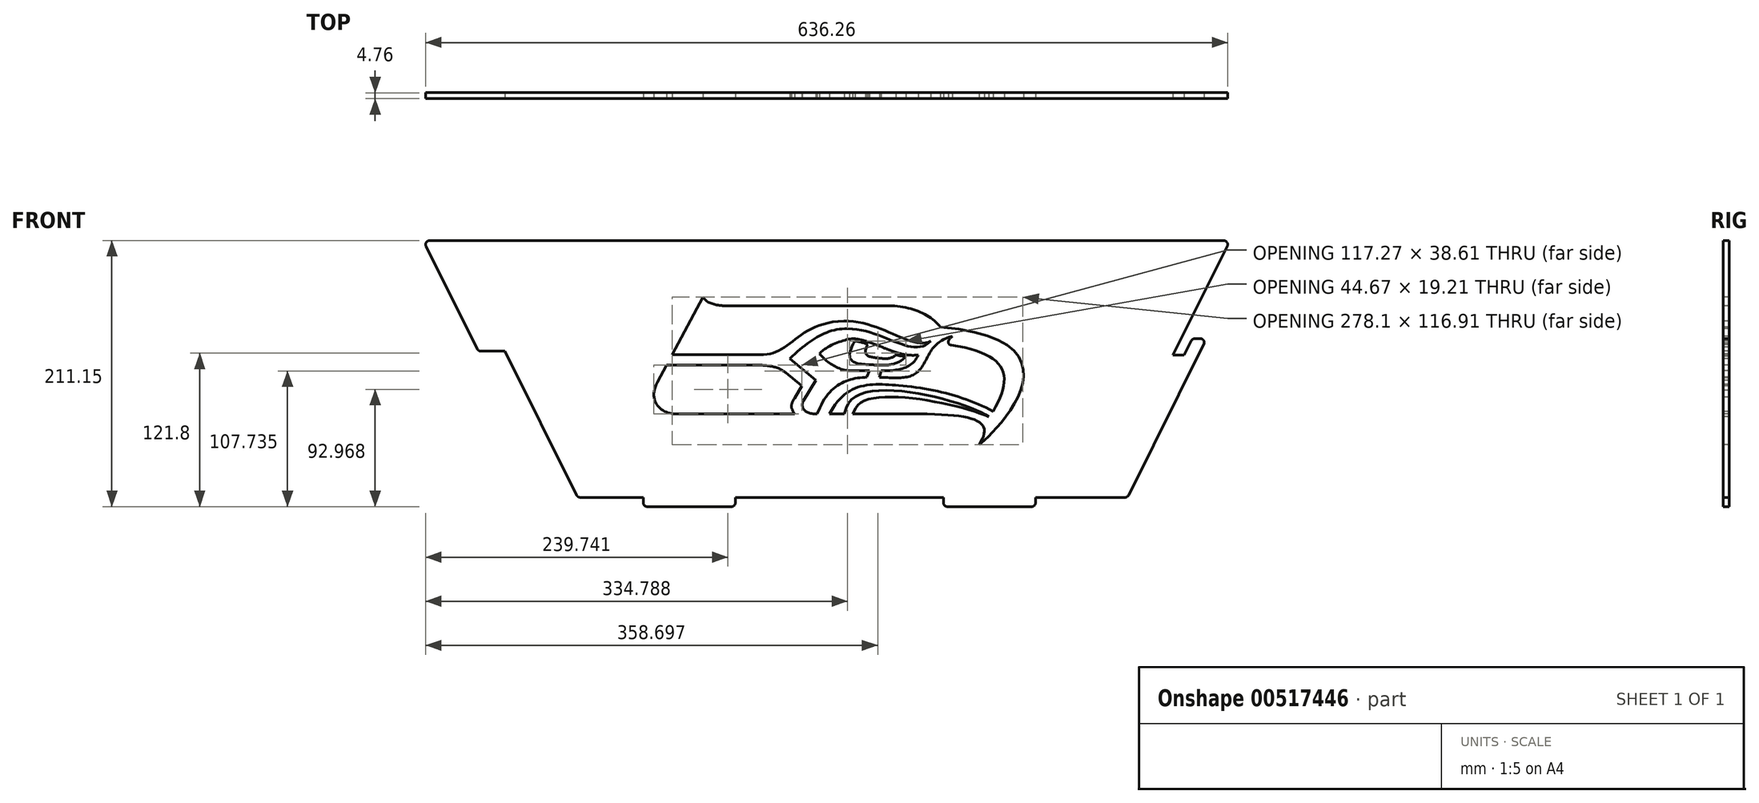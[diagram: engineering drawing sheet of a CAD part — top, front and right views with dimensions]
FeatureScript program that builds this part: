
annotation { "Feature Type Name" : "Feature", "Feature Type Description" : "" }
export const myFeature = defineFeature(function(context is Context, id is Id, definition is map)
    precondition{}
    {
        {
            var Q0;
            Q0=qCreatedBy(makeId("Front.planeOp"),FACE);
            var sketch = newSketch(context, id + "F0", { "sketchPlane" : qUnion([Q0])});
            skLineSegment(sketch, "E0", {"start": v(-309.98, 203.78) * mm, "end": v(304.85, 203.78) * mm});
            skLineSegment(sketch, "E1", {"start": v(289.12, 121.39) * mm, "end": v(229.48, 1.76) * mm});
            skLineSegment(sketch, "E2", {"start": v(226.64, 0) * mm, "end": v(155.58, 0) * mm});
            skLineSegment(sketch, "E3", {"start": v(0, 0) * mm, "end": v(0, 203.78) * mm, "construction": true});
            skLineSegment(sketch, "E4", {"start": v(-155.58, 0) * mm, "end": v(-155.58, -4.2) * mm});
            skLineSegment(sketch, "E5", {"start": v(-152.4, -7.37) * mm, "end": v(-85.73, -7.37) * mm});
            skLineSegment(sketch, "E6", {"start": v(-82.55, -4.2) * mm, "end": v(-82.55, 0) * mm});
            skLineSegment(sketch, "E7", {"start": v(82.55, 0) * mm, "end": v(82.55, -4.2) * mm});
            skLineSegment(sketch, "E8", {"start": v(85.73, -7.37) * mm, "end": v(152.4, -7.37) * mm});
            skLineSegment(sketch, "E9", {"start": v(155.58, -4.2) * mm, "end": v(155.58, 0) * mm});
            skLineSegment(sketch, "E10", {"start": v(279.18, 124.22) * mm, "end": v(273.51, 112.85) * mm});
            skLineSegment(sketch, "E11", {"start": v(273.51, 112.85) * mm, "end": v(264.64, 112.85) * mm});
            skLineSegment(sketch, "E12", {"start": v(264.64, 112.85) * mm, "end": v(307.69, 199.19) * mm});
            skLineSegment(sketch, "E13", {"start": v(282.02, 125.98) * mm, "end": v(286.28, 125.98) * mm});
            skArc(sketch, "E14.filletArc", {"start": v(282.02, 125.98) * mm, "mid": v(280.35, 125.5) * mm, "end": v(279.18, 124.22) * mm});
            skArc(sketch, "E15.filletArc", {"start": v(289.12, 121.39) * mm, "mid": v(288.98, 124.47) * mm, "end": v(286.28, 125.98) * mm});
            skLineSegment(sketch, "E16", {"start": v(-284.48, 116.03) * mm, "end": v(-265.5, 116.03) * mm});
            skLineSegment(sketch, "E17", {"start": v(-287.33, 117.79) * mm, "end": v(-327.91, 199.19) * mm});
            skLineSegment(sketch, "E18", {"start": v(-309.98, 203.78) * mm, "end": v(-325.07, 203.78) * mm});
            skLineSegment(sketch, "E19", {"start": v(264.64, 112.85) * mm, "end": v(-263.91, 112.85) * mm, "construction": true});
            skPoint(sketch, "E20.visualSharp", {"position": v(-330.2, 203.78) * mm});
            skArc(sketch, "E20.filletArc", {"start": v(-325.07, 203.78) * mm, "mid": v(-327.77, 202.27) * mm, "end": v(-327.91, 199.19) * mm});
            skPoint(sketch, "E21.visualSharp", {"position": v(-286.45, 116.03) * mm});
            skArc(sketch, "E21.filletArc", {"start": v(-287.33, 117.79) * mm, "mid": v(-286.16, 116.5) * mm, "end": v(-284.48, 116.03) * mm});
            skLineSegment(sketch, "E22", {"start": v(-286.45, 116.03) * mm, "end": v(-228.6, 0) * mm, "construction": true});
            skLineSegment(sketch, "E23", {"start": v(-309.24, 203.78) * mm, "end": v(-208.52, 1.76) * mm, "construction": true});
            skLineSegment(sketch, "E24", {"start": v(-228.6, 0) * mm, "end": v(-207.64, 0) * mm, "construction": true});
            skLineSegment(sketch, "E25.trimOffspring", {"start": v(-155.58, 0) * mm, "end": v(-205.68, 0) * mm});
            skLineSegment(sketch, "E26.trimOffspring", {"start": v(82.55, 0) * mm, "end": v(-82.55, 0) * mm});
            skLineSegment(sketch, "E27", {"start": v(-265.5, 116.03) * mm, "end": v(-207.64, 0) * mm});
            skPoint(sketch, "E28.visualSharp", {"position": v(-155.58, -7.37) * mm});
            skArc(sketch, "E28.filletArc", {"start": v(-155.58, -4.2) * mm, "mid": v(-154.65, -6.44) * mm, "end": v(-152.4, -7.37) * mm});
            skPoint(sketch, "E29.visualSharp", {"position": v(-82.55, -7.37) * mm});
            skArc(sketch, "E29.filletArc", {"start": v(-85.73, -7.37) * mm, "mid": v(-83.48, -6.44) * mm, "end": v(-82.55, -4.2) * mm});
            skPoint(sketch, "E30.visualSharp", {"position": v(82.55, -7.37) * mm});
            skArc(sketch, "E30.filletArc", {"start": v(82.55, -4.2) * mm, "mid": v(83.48, -6.44) * mm, "end": v(85.73, -7.37) * mm});
            skPoint(sketch, "E31.visualSharp", {"position": v(155.58, -7.37) * mm});
            skArc(sketch, "E31.filletArc", {"start": v(152.4, -7.37) * mm, "mid": v(154.65, -6.44) * mm, "end": v(155.58, -4.2) * mm});
            skPoint(sketch, "E32.visualSharp", {"position": v(-207.64, 0) * mm});
            skPoint(sketch, "E33.visualSharp", {"position": v(228.6, 0) * mm});
            skPoint(sketch, "E34.visualSharp", {"position": v(309.98, 203.78) * mm});
            skArc(sketch, "E34.filletArc", {"start": v(307.69, 199.19) * mm, "mid": v(307.55, 202.27) * mm, "end": v(304.85, 203.78) * mm});
            skLineSegment(sketch, "E35", {"start": v(289.12, 121.39) * mm, "end": v(330.2, 203.78) * mm, "construction": true});
            skLineSegment(sketch, "E36", {"start": v(330.2, 203.78) * mm, "end": v(304.85, 203.78) * mm, "construction": true});
            skArc(sketch, "E37.filletArc", {"start": v(226.64, 0) * mm, "mid": v(228.3, 0.48) * mm, "end": v(229.48, 1.76) * mm});
            skArc(sketch, "E38.filletArc", {"start": v(-208.52, 1.76) * mm, "mid": v(-207.35, 0.48) * mm, "end": v(-205.68, 0) * mm});
            skSolve(sketch);
        }
        {
            var Q0;
            Q0 = qSketchRegion(id + "F0", true);
            extrude(context, id + "F1", {"entities" : qUnion([Q0]), "oppositeDirection" : true, "depth" : 4.76 * mm, "offsetDistance" : 25.4 * mm});
        }
        {
            var Q0;
            Q0=makeQuery(id+"F1.opExtrude","CAP_FACE",FACE,{"disambiguationData":[OSD([sQuery(id+"F0.wireOp",EDGE,"E0"),sQuery(id+"F0.wireOp",EDGE,"E1"),sQuery(id+"F0.wireOp",EDGE,"E2"),sQuery(id+"F0.wireOp",EDGE,"E4"),sQuery(id+"F0.wireOp",EDGE,"E5"),sQuery(id+"F0.wireOp",EDGE,"E6"),sQuery(id+"F0.wireOp",EDGE,"E7"),sQuery(id+"F0.wireOp",EDGE,"E8"),sQuery(id+"F0.wireOp",EDGE,"E9"),sQuery(id+"F0.wireOp",EDGE,"E10"),sQuery(id+"F0.wireOp",EDGE,"E11"),sQuery(id+"F0.wireOp",EDGE,"E12"),sQuery(id+"F0.wireOp",EDGE,"E13"),sQuery(id+"F0.wireOp",EDGE,"E14.filletArc"),sQuery(id+"F0.wireOp",EDGE,"E15.filletArc"),sQuery(id+"F0.wireOp",EDGE,"E16"),sQuery(id+"F0.wireOp",EDGE,"E17"),sQuery(id+"F0.wireOp",EDGE,"E18"),sQuery(id+"F0.wireOp",EDGE,"E20.filletArc"),sQuery(id+"F0.wireOp",EDGE,"E21.filletArc"),sQuery(id+"F0.wireOp",EDGE,"E25.trimOffspring"),sQuery(id+"F0.wireOp",EDGE,"E26.trimOffspring"),sQuery(id+"F0.wireOp",EDGE,"E27"),sQuery(id+"F0.wireOp",EDGE,"E28.filletArc"),sQuery(id+"F0.wireOp",EDGE,"E29.filletArc"),sQuery(id+"F0.wireOp",EDGE,"E30.filletArc"),sQuery(id+"F0.wireOp",EDGE,"E31.filletArc"),sQuery(id+"F0.wireOp",EDGE,"E34.filletArc")])],"isStart":true});
            var sketch = newSketch(context, id + "F2", { "sketchPlane" : qUnion([Q0])});
            skLineSegment(sketch, "E39", {"start": v(0, 0) * mm, "end": v(0, 203.78) * mm, "construction": true});
            skLineSegment(sketch, "E40", {"start": v(0, 167.71) * mm, "end": v(0, 33.27) * mm, "construction": true});
            skLineSegment(sketch, "E41", {"start": v(-108.09, 158.82) * mm, "end": v(-132.5, 113.35) * mm});
            skLineSegment(sketch, "E42", {"start": v(-130.23, 66.3) * mm, "end": v(-35.6, 66.3) * mm});
            skLineSegment(sketch, "E43", {"start": v(39.49, 151.96) * mm, "end": v(-89.13, 151.96) * mm});
            skFitSpline(sketch, "E44", {"points": [v(-144.4, 91.19) * mm, v(-130.23, 66.3) * mm], "startDerivative": vector(-23.62, -43.99) * mm, "endDerivative": vector(34.53, 0) * mm});
            skFitSpline(sketch, "E45", {"points": [v(-108.09, 158.82) * mm, v(-89.13, 151.96) * mm], "startDerivative": vector(9.52, -18.99) * mm, "endDerivative": vector(11.02, 0) * mm});
            skFitSpline(sketch, "E46", {"points": [v(39.49, 151.96) * mm, v(80.15, 135.2) * mm], "startDerivative": vector(51.44, 0) * mm, "endDerivative": vector(23.97, -30.42) * mm});
            skFitSpline(sketch, "E47", {"points": [v(80.15, 135.2) * mm, v(110.88, 41.9) * mm], "startDerivative": vector(360.12, -30.49) * mm, "endDerivative": vector(-33.86, -25.2) * mm});
            skFitSpline(sketch, "E48", {"points": [v(56.6, 66.3) * mm, v(110.88, 41.9) * mm], "startDerivative": vector(161.76, 0) * mm, "endDerivative": vector(-35.05, -56.56) * mm});
            skLineSegment(sketch, "E49", {"start": v(-137.04, 104.9) * mm, "end": v(-63.89, 104.9) * mm});
            skFitSpline(sketch, "E50", {"points": [v(-63.89, 104.9) * mm, v(-42.6, 98.92) * mm], "startDerivative": vector(29.3, 0) * mm, "endDerivative": vector(14.25, -11.8) * mm});
            skLineSegment(sketch, "E51", {"start": v(-42.6, 98.92) * mm, "end": v(-29.87, 88.38) * mm});
            skLineSegment(sketch, "E52", {"start": v(-29.87, 88.38) * mm, "end": v(-35.6, 78.74) * mm});
            skFitSpline(sketch, "E53", {"points": [v(-35.6, 78.74) * mm, v(-35.6, 66.3) * mm], "startDerivative": vector(-10.08, -16.94) * mm, "endDerivative": vector(9.5, -15.27) * mm});
            skLineSegment(sketch, "E54", {"start": v(-132.5, 113.35) * mm, "end": v(-60.21, 113.35) * mm});
            skLineSegment(sketch, "E55.trimOffspring", {"start": v(-137.04, 104.9) * mm, "end": v(-144.4, 91.19) * mm});
            skLineSegment(sketch, "E56", {"start": v(-132.5, 113.35) * mm, "end": v(-137.04, 104.9) * mm, "construction": true});
            skFitSpline(sketch, "E57", {"points": [v(-60.21, 113.35) * mm, v(3.5, 139.84) * mm], "startDerivative": vector(63.1, 0) * mm, "endDerivative": vector(107.2, 1.94) * mm});
            skFitSpline(sketch, "E58", {"points": [v(3.5, 139.84) * mm, v(72.6, 124.07) * mm], "startDerivative": vector(90.38, 1.64) * mm, "endDerivative": vector(45.22, 23.83) * mm});
            skFitSpline(sketch, "E59", {"points": [v(72.6, 124.07) * mm, v(6.52, 133.86) * mm], "startDerivative": vector(-45.64, -45.32) * mm, "endDerivative": vector(-85.94, 0.42) * mm});
            skFitSpline(sketch, "E60", {"points": [v(6.52, 133.86) * mm, v(-39.46, 110.17) * mm], "startDerivative": vector(-51.76, 0.25) * mm, "endDerivative": vector(-48.45, -45.08) * mm});
            skLineSegment(sketch, "E61", {"start": v(-39.46, 110.17) * mm, "end": v(-18.8, 93.06) * mm});
            skLineSegment(sketch, "E62", {"start": v(-18.8, 93.06) * mm, "end": v(-28.53, 76.72) * mm});
            skFitSpline(sketch, "E63", {"points": [v(-28.53, 76.72) * mm, v(-19.85, 66.3) * mm], "startDerivative": vector(-7.73, -12.98) * mm, "endDerivative": vector(25.06, 0) * mm});
            skLineSegment(sketch, "E64.trimOffspring", {"start": v(-19.85, 66.3) * mm, "end": v(-17.7, 66.3) * mm});
            skLineSegment(sketch, "E65", {"start": v(-35.6, 66.3) * mm, "end": v(-19.85, 66.3) * mm, "construction": true});
            skLineSegment(sketch, "E66", {"start": v(-15.54, 71.12) * mm, "end": v(-4.96, 71.12) * mm});
            skFitSpline(sketch, "E67", {"points": [v(12.96, 71.12) * mm, v(118.51, 64.03) * mm], "startDerivative": vector(28.3, 55.79) * mm, "endDerivative": vector(66.83, -29.51) * mm});
            skFitSpline(sketch, "E68", {"points": [v(118.51, 64.03) * mm, v(5.37, 71.12) * mm], "startDerivative": vector(-50.89, 35.62) * mm, "endDerivative": vector(-29.24, -87.9) * mm});
            skLineSegment(sketch, "E69.trimOffspring", {"start": v(5.37, 71.12) * mm, "end": v(12.96, 71.12) * mm});
            skFitSpline(sketch, "E70", {"points": [v(121.98, 68.24) * mm, v(88.5, 120.82) * mm], "startDerivative": vector(50.2, 86.85) * mm, "endDerivative": vector(-135.02, 20.7) * mm});
            skFitSpline(sketch, "E71", {"points": [v(88.5, 120.82) * mm, v(89.53, 127.83) * mm], "startDerivative": vector(-5.03, 0.77) * mm, "endDerivative": vector(15.52, 12.08) * mm});
            skFitSpline(sketch, "E72", {"points": [v(89.53, 127.83) * mm, v(62.13, 99.58) * mm], "startDerivative": vector(-60.05, -16.28) * mm, "endDerivative": vector(-28.65, -26.97) * mm});
            skFitSpline(sketch, "E73", {"points": [v(62.13, 99.58) * mm, v(-15.54, 71.12) * mm], "startDerivative": vector(-46.14, -43.42) * mm, "endDerivative": vector(-55.27, -124.04) * mm});
            skFitSpline(sketch, "E74", {"points": [v(-4.96, 71.12) * mm, v(47.06, 88.77) * mm], "startDerivative": vector(37.66, 62.1) * mm, "endDerivative": vector(60.54, -5) * mm});
            skFitSpline(sketch, "E75", {"points": [v(47.06, 88.77) * mm, v(121.98, 68.24) * mm], "startDerivative": vector(78.03, -6.45) * mm, "endDerivative": vector(65.33, -35.8) * mm});
            skLineSegment(sketch, "E76", {"start": v(13.4, 125.77) * mm, "end": v(13.4, 125.77) * mm});
            skFitSpline(sketch, "E77", {"points": [v(-15.77, 113.85) * mm, v(9.36, 100.42) * mm], "startDerivative": vector(19.67, -22.95) * mm, "endDerivative": vector(26.78, 0) * mm});
            skFitSpline(sketch, "E78", {"points": [v(13.4, 125.77) * mm, v(62.58, 113) * mm], "startDerivative": vector(56.9, -10.33) * mm, "endDerivative": vector(52.2, 6.25) * mm});
            skFitSpline(sketch, "E79", {"points": [v(62.58, 113) * mm, v(35.67, 100.42) * mm], "startDerivative": vector(-15.1, -33.9) * mm, "endDerivative": vector(-27.67, 0) * mm});
            skLineSegment(sketch, "E80", {"start": v(9.36, 100.42) * mm, "end": v(35.67, 100.42) * mm});
            skFitSpline(sketch, "E81", {"points": [v(13.4, 125.77) * mm, v(29.08, 105.02) * mm], "startDerivative": vector(-42.96, -65.33) * mm, "endDerivative": vector(36.12, -2.5) * mm});
            skFitSpline(sketch, "E82", {"points": [v(29.08, 105.02) * mm, v(53.78, 113.03) * mm], "startDerivative": vector(19.14, -1.32) * mm, "endDerivative": vector(20.65, 26.69) * mm});
            skFitSpline(sketch, "E83", {"points": [v(30.22, 120.66) * mm, v(42.58, 115.82) * mm], "startDerivative": vector(-13.87, -23.66) * mm, "endDerivative": vector(8.7, 16.26) * mm});
            skLineSegment(sketch, "E84", {"start": v(23.72, 123.06) * mm, "end": v(23.72, 123.06) * mm});
            skFitSpline(sketch, "E85", {"points": [v(31.94, 110.44) * mm, v(45.67, 114.8) * mm], "startDerivative": vector(14.23, -1.96) * mm, "endDerivative": vector(7.76, 16.18) * mm});
            skFitSpline(sketch, "E86", {"points": [v(23.72, 123.06) * mm, v(31.94, 110.44) * mm], "startDerivative": vector(-25.5, -36.53) * mm, "endDerivative": vector(17.6, -2.42) * mm});
            skFitSpline(sketch, "E87", {"points": [v(13.4, 125.77) * mm, v(-15.77, 113.85) * mm], "startDerivative": vector(-21.85, 3.96) * mm, "endDerivative": vector(-10.38, -16.94) * mm});
            skFitSpline(sketch, "E88", {"points": [v(13.4, 125.77) * mm, v(62.58, 113) * mm], "startDerivative": vector(56.9, -10.33) * mm, "endDerivative": vector(52.2, 6.25) * mm, "construction": true});
            skFitSpline(sketch, "E89", {"points": [v(13.4, 125.77) * mm, v(62.58, 113) * mm], "startDerivative": vector(56.9, -10.33) * mm, "endDerivative": vector(52.2, 6.25) * mm});
            skFitSpline(sketch, "E90", {"points": [v(13.4, 125.77) * mm, v(62.58, 113) * mm], "startDerivative": vector(56.9, -10.33) * mm, "endDerivative": vector(52.2, 6.25) * mm});
            skLineSegment(sketch, "E91", {"start": v(-15.54, 71.12) * mm, "end": v(-17.7, 66.3) * mm});
            skLineSegment(sketch, "E92", {"start": v(-4.96, 71.12) * mm, "end": v(-7.89, 66.3) * mm});
            skLineSegment(sketch, "E93", {"start": v(5.37, 71.12) * mm, "end": v(3.76, 66.3) * mm});
            skLineSegment(sketch, "E94", {"start": v(12.96, 71.12) * mm, "end": v(10.52, 66.3) * mm});
            skLineSegment(sketch, "E95", {"start": v(-17.7, 66.3) * mm, "end": v(-7.89, 66.3) * mm, "construction": true});
            skLineSegment(sketch, "E96", {"start": v(-7.89, 66.3) * mm, "end": v(3.76, 66.3) * mm});
            skLineSegment(sketch, "E97", {"start": v(3.76, 66.3) * mm, "end": v(10.52, 66.3) * mm, "construction": true});
            skLineSegment(sketch, "E98", {"start": v(10.52, 66.3) * mm, "end": v(56.6, 66.3) * mm});
            skLineSegment(sketch, "E99", {"start": v(25.96, 105.18) * mm, "end": v(21.8, 95.37) * mm});
            skLineSegment(sketch, "E100", {"start": v(33.83, 104.83) * mm, "end": v(31.94, 95.28) * mm});
            skFitSpline(sketch, "E101", {"points": [v(12.3, 124.03) * mm, v(22.5, 121.19) * mm], "startDerivative": vector(13, -1.36) * mm, "endDerivative": vector(6, -3.24) * mm});
            skFitSpline(sketch, "E102", {"points": [v(44.74, 113.3) * mm, v(52.8, 111.85) * mm], "startDerivative": vector(6.28, -2.9) * mm, "endDerivative": vector(9.66, -0.77) * mm});
            skSolve(sketch);
        }
        {
            var Q0;
            Q0=makeQuery(id+"F2.imprint","IMPRINT",FACE,{"disambiguationData":[TD([[makeQuery(id+"F2.imprint","IMPRINT",EDGE,{"derivedFrom":sQuery(id+"F2.wireOp",EDGE,"E42")}),1.0]])]});
            var Q1;
            Q1=makeQuery(id+"F2.imprint","IMPRINT",FACE,{"disambiguationData":[TD([[makeQuery(id+"F2.imprint","IMPRINT",EDGE,{"derivedFrom":sQuery(id+"F2.wireOp",EDGE,"E41")}),1.0]])]});
            var Q2;
            {var subQ0=sQuery(id+"F2.wireOp",EDGE,"E101");Q2=makeQuery(id+"F2.imprint","IMPRINT",FACE,{"disambiguationData":[TD([[makeQuery(id+"F2.imprint","IMPRINT",EDGE,{"derivedFrom":subQ0}),-1.0]])]});}
            var Q3;
            {var subQ5=sQuery(id+"F2.wireOp",EDGE,"E81");var subQ9=sQuery(id+"F2.wireOp",EDGE,"E82");var subQ10=makeQuery(id+"F2.imprint","INTERSECT",VERTEX,{"derivedFrom":[subQ5,subQ9]});Q3=makeQuery(id+"F2.imprint","IMPRINT",FACE,{"disambiguationData":[TD([[makeQuery(id+"F2.imprint","IMPRINT",EDGE,{"disambiguationData":[TD([[subQ10,1.0]])],"derivedFrom":subQ5}),1.0]])]});}
            var Q4;
            {var subQ0=sQuery(id+"F2.wireOp",EDGE,"E102");Q4=makeQuery(id+"F2.imprint","IMPRINT",FACE,{"disambiguationData":[TD([[makeQuery(id+"F2.imprint","IMPRINT",EDGE,{"derivedFrom":subQ0}),-1.0]])]});}
            extrude(context, id + "F3", {"entities" : qUnion([Q0, Q1, Q2, Q3, Q4]), "operationType" : NewBodyOperationType.REMOVE, "endBound" : BoundingType.THROUGH_ALL, "oppositeDirection" : true, "depth" : 25.4 * mm, "offsetDistance" : 25.4 * mm});
        }
    });
